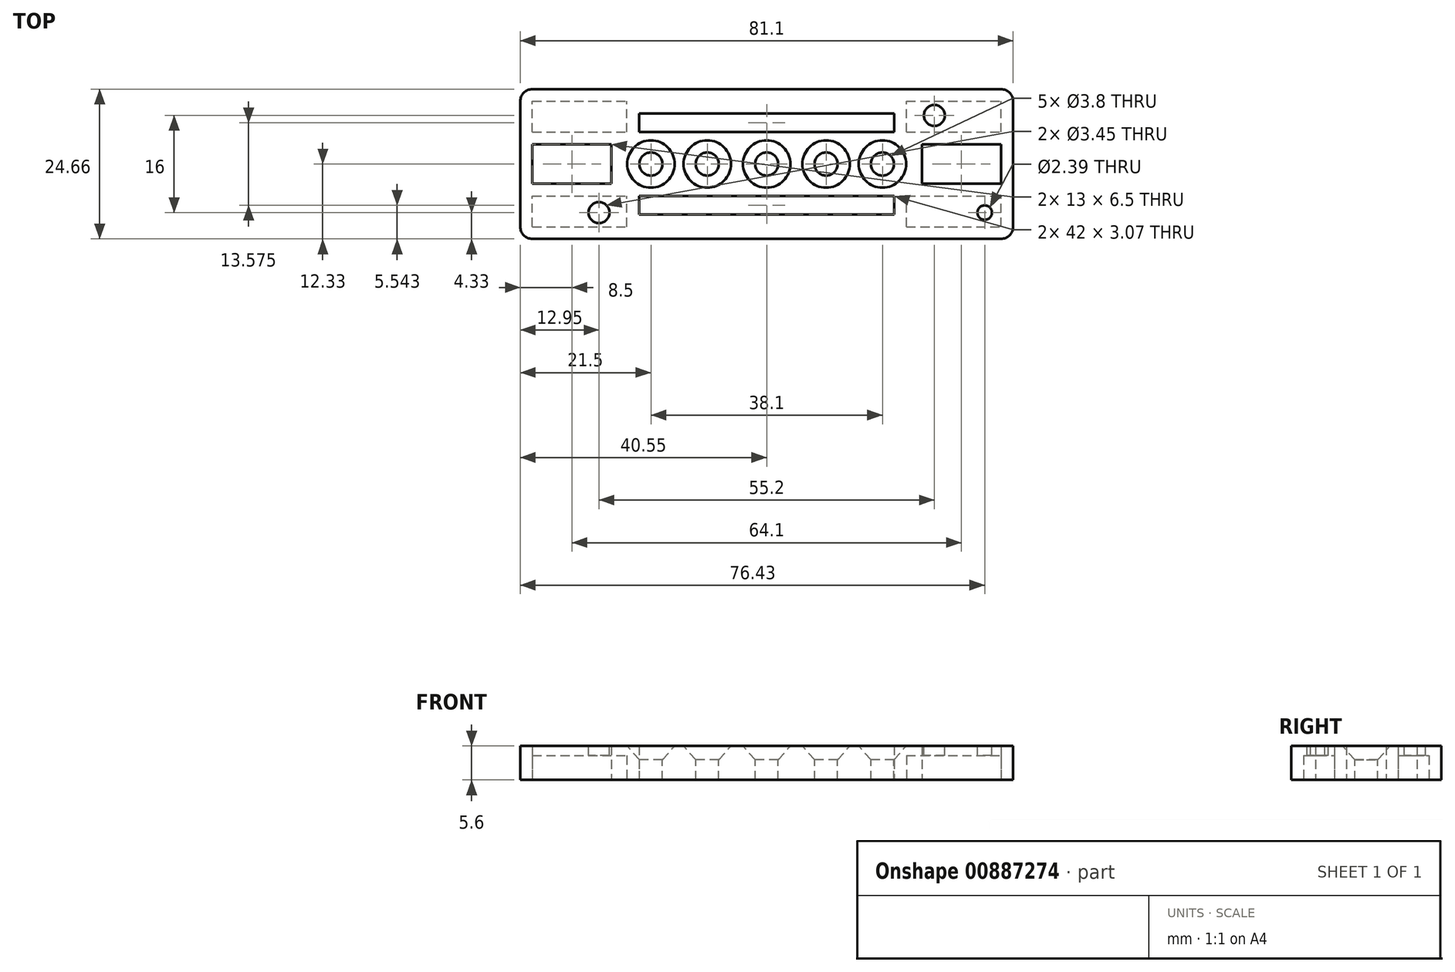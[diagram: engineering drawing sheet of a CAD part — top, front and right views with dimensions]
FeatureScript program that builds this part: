
annotation { "Feature Type Name" : "Feature", "Feature Type Description" : "" }
export const myFeature = defineFeature(function(context is Context, id is Id, definition is map)
    precondition{}
    {
        {
            var Q0;
            Q0=qCreatedBy(makeId("Top.planeOp"),FACE);
            var sketch = newSketch(context, id + "F0", { "sketchPlane" : qUnion([Q0])});
            skLineSegment(sketch, "E0.left", {"start": v(40.55, -12.33) * mm, "end": v(40.55, 12.32) * mm});
            skPoint(sketch, "E0.middle", {"position": v(0, 0) * mm});
            skLineSegment(sketch, "E1.bottom", {"start": v(-40.55, 12.33) * mm, "end": v(40.55, 12.32) * mm});
            skLineSegment(sketch, "E1.top", {"start": v(-40.55, -12.32) * mm, "end": v(40.55, -12.32) * mm});
            skLineSegment(sketch, "E1.left", {"start": v(-40.55, 12.33) * mm, "end": v(-40.55, -12.32) * mm});
            skLineSegment(sketch, "E2.bottom", {"start": v(38.55, -10.33) * mm, "end": v(-38.55, -10.32) * mm, "construction": true});
            skLineSegment(sketch, "E2.top", {"start": v(38.55, 10.32) * mm, "end": v(-38.55, 10.33) * mm, "construction": true});
            skLineSegment(sketch, "E2.left", {"start": v(38.55, -10.33) * mm, "end": v(38.55, 10.32) * mm, "construction": true});
            skLineSegment(sketch, "E2.right", {"start": v(-38.55, -10.32) * mm, "end": v(-38.55, 10.33) * mm, "construction": true});
            skSolve(sketch);
        }
        {
            var Q0;
            Q0=makeQuery(id+"F0.imprint","IMPRINT",FACE,{"disambiguationData":[TD([[makeQuery(id+"F0.imprint","IMPRINT",EDGE,{"derivedFrom":sQuery(id+"F0.wireOp",EDGE,"0eb0cbb2-3808-4bd1-ae6b-da4b1fe55920")}),-1.0]])]});
            var Q1;
            Q1=makeQuery(id+"F0.imprint","IMPRINT",FACE,{"disambiguationData":[TD([[makeQuery(id+"F0.imprint","IMPRINT",EDGE,{"derivedFrom":sQuery(id+"F0.wireOp",EDGE,"E0.left")}),1.0]])]});
            extrude(context, id + "F1", {"entities" : qUnion([Q0, Q1]), "depth" : 5.6 * mm, "offsetDistance" : 25 * mm});
        }
        {
            var Q0;
            Q0=makeQuery(id+"F1.opExtrude","CAP_FACE",FACE,{"disambiguationData":[OSD([sQuery(id+"F0.wireOp",EDGE,"E0.left"),sQuery(id+"F0.wireOp",EDGE,"E1.bottom"),sQuery(id+"F0.wireOp",EDGE,"E1.top"),sQuery(id+"F0.wireOp",EDGE,"E1.left")])],"isStart":false});
            var sketch = newSketch(context, id + "F2", { "sketchPlane" : qUnion([Q0])});
            skLineSegment(sketch, "E3.0.0", {"start": v(40.55, 12.32) * mm, "end": v(-40.55, 12.33) * mm});
            skLineSegment(sketch, "E3.0.1", {"start": v(-40.55, 12.33) * mm, "end": v(-40.55, -12.32) * mm});
            skLineSegment(sketch, "E3.0.2", {"start": v(-40.55, -12.32) * mm, "end": v(40.55, -12.32) * mm});
            skLineSegment(sketch, "E3.0.3", {"start": v(40.55, -12.32) * mm, "end": v(40.55, 12.32) * mm});
            skLineSegment(sketch, "E4.bottom", {"start": v(35.88, -8) * mm, "end": v(-27.6, -8) * mm, "construction": true});
            skLineSegment(sketch, "E4.top", {"start": v(27.6, 8) * mm, "end": v(-27.6, 8) * mm, "construction": true});
            skLineSegment(sketch, "E4.right", {"start": v(-27.6, -8) * mm, "end": v(-27.6, 8) * mm, "construction": true});
            skLineSegment(sketch, "E5", {"start": v(-27.6, 8) * mm, "end": v(-27.6, 12.33) * mm, "construction": true});
            skLineSegment(sketch, "E6", {"start": v(-27.6, -8) * mm, "end": v(-27.6, -12.32) * mm, "construction": true});
            skLineSegment(sketch, "E7", {"start": v(-27.6, 8) * mm, "end": v(-40.55, 8) * mm, "construction": true});
            skLineSegment(sketch, "E8", {"start": v(27.6, 8) * mm, "end": v(40.55, 8) * mm, "construction": true});
            skSolve(sketch);
        }
        {
            var Q0;
            Q0=sQuery(id+"F2.wireOp",VERTEX,"E4.bottom.end");
            var Q1;
            Q1=sQuery(id+"F2.wireOp",VERTEX,"E4.top.start");
            var Q2;
            Q2=makeQuery(id+"F1.opExtrude","SWEPT_BODY",BODY,{"disambiguationData":[OSD([sQuery(id+"F0.wireOp",EDGE,"E0.left"),sQuery(id+"F0.wireOp",EDGE,"E1.bottom"),sQuery(id+"F0.wireOp",EDGE,"E1.top"),sQuery(id+"F0.wireOp",EDGE,"E1.left")])]});
            hole(context, id + "F3", {"style" : HoleStyle.SIMPLE, "endStyle" : HoleEndStyle.THROUGH, "holeDiameter" : 3.45 * mm, "majorDiameter" : 5 * mm, "isTappedThrough" : true, "tappedDepth" : 12 * mm, "tapClearance" : 3, "locations" : qUnion([Q0, Q1]), "scope" : qUnion([Q2])});
        }
        {
            var Q0;
            Q0=sQuery(id+"F2.wireOp",VERTEX,"E4.bottom.start");
            var Q1;
            Q1=makeQuery(id+"F1.opExtrude","SWEPT_BODY",BODY,{"disambiguationData":[OSD([sQuery(id+"F0.wireOp",EDGE,"E0.left"),sQuery(id+"F0.wireOp",EDGE,"E1.bottom"),sQuery(id+"F0.wireOp",EDGE,"E1.top"),sQuery(id+"F0.wireOp",EDGE,"E1.left")])]});
            hole(context, id + "F4", {"style" : HoleStyle.SIMPLE, "endStyle" : HoleEndStyle.THROUGH, "holeDiameter" : 2.4 * mm, "majorDiameter" : 5 * mm, "isTappedThrough" : true, "tappedDepth" : 12 * mm, "tapClearance" : 3, "locations" : qUnion([Q0]), "scope" : qUnion([Q1])});
        }
        {
            var Q0;
            Q0=makeQuery(id+"F2.imprint","IMPRINT",FACE,{"disambiguationData":[TD([[makeQuery(id+"F2.imprint","IMPRINT",EDGE,{"derivedFrom":sQuery(id+"F2.wireOp",EDGE,"E3.0.0")}),-1.0]])]});
            var sketch = newSketch(context, id + "F5", { "sketchPlane" : qUnion([Q0])});
            skLineSegment(sketch, "E9", {"start": v(0, 0) * mm, "end": v(-9.78, 0) * mm, "construction": true});
            skLineSegment(sketch, "E10", {"start": v(-9.78, 0) * mm, "end": v(-19.05, 0) * mm, "construction": true});
            skLineSegment(sketch, "E11", {"start": v(0, 0) * mm, "end": v(9.78, 0) * mm, "construction": true});
            skLineSegment(sketch, "E12", {"start": v(9.78, 0) * mm, "end": v(19.05, 0) * mm, "construction": true});
            skSolve(sketch);
        }
        {
            var Q0;
            Q0=sQuery(id+"F5.wireOp",VERTEX,"E10.end");
            var Q1;
            Q1=sQuery(id+"F5.wireOp",VERTEX,"E9.end");
            var Q2;
            Q2=sQuery(id+"F5.wireOp",VERTEX,"E9.start");
            var Q3;
            Q3=sQuery(id+"F5.wireOp",VERTEX,"E11.end");
            var Q4;
            Q4=sQuery(id+"F5.wireOp",VERTEX,"E12.end");
            var Q5;
            Q5=makeQuery(id+"F1.opExtrude","SWEPT_BODY",BODY,{"disambiguationData":[OSD([sQuery(id+"F0.wireOp",EDGE,"E0.left"),sQuery(id+"F0.wireOp",EDGE,"E1.bottom"),sQuery(id+"F0.wireOp",EDGE,"E1.top"),sQuery(id+"F0.wireOp",EDGE,"E1.left")])]});
            hole(context, id + "F6", {"style" : HoleStyle.C_SINK, "endStyle" : HoleEndStyle.THROUGH, "holeDiameter" : 3.8 * mm, "cSinkDiameter" : 7.8 * mm, "cSinkAngle" : 82 * degree, "majorDiameter" : 5 * mm, "isTappedThrough" : true, "tappedDepth" : 12 * mm, "tapClearance" : 3, "locations" : qUnion([Q0, Q1, Q2, Q3, Q4]), "scope" : qUnion([Q5])});
        }
        {
            var Q0;
            Q0=makeQuery(id+"F1.opExtrude","CAP_FACE",FACE,{"disambiguationData":[OSD([sQuery(id+"F0.wireOp",EDGE,"E0.left"),sQuery(id+"F0.wireOp",EDGE,"E1.bottom"),sQuery(id+"F0.wireOp",EDGE,"E1.top"),sQuery(id+"F0.wireOp",EDGE,"E1.left")])],"isStart":true});
            var sketch = newSketch(context, id + "F7", { "sketchPlane" : qUnion([Q0])});
            skLineSegment(sketch, "E13.0.0", {"start": v(-40.55, -12.33) * mm, "end": v(40.55, -12.32) * mm});
            skLineSegment(sketch, "E13.0.1", {"start": v(40.55, -12.32) * mm, "end": v(40.55, 12.33) * mm});
            skLineSegment(sketch, "E13.0.2", {"start": v(40.55, 12.32) * mm, "end": v(-40.55, 12.32) * mm});
            skLineSegment(sketch, "E13.0.3", {"start": v(-40.55, 12.32) * mm, "end": v(-40.55, -12.33) * mm});
            skLineSegment(sketch, "E14", {"start": v(-40.55, 5.25) * mm, "end": v(40.55, 5.25) * mm});
            skLineSegment(sketch, "E15", {"start": v(-40.55, -5.25) * mm, "end": v(40.55, -5.25) * mm});
            skLineSegment(sketch, "E16.bottom", {"start": v(-38.55, 10.32) * mm, "end": v(38.55, 10.32) * mm});
            skLineSegment(sketch, "E16.top", {"start": v(-38.55, -10.33) * mm, "end": v(38.55, -10.32) * mm});
            skLineSegment(sketch, "E16.left", {"start": v(-38.55, 10.32) * mm, "end": v(-38.55, -10.33) * mm});
            skLineSegment(sketch, "E16.right", {"start": v(38.55, 10.33) * mm, "end": v(38.55, -10.32) * mm});
            skLineSegment(sketch, "E17", {"start": v(-23, 10.32) * mm, "end": v(-23, 5.25) * mm});
            skLineSegment(sketch, "E18", {"start": v(-21, 10.32) * mm, "end": v(-21, 5.25) * mm});
            skLineSegment(sketch, "E19", {"start": v(21, 10.33) * mm, "end": v(21, 5.25) * mm});
            skLineSegment(sketch, "E20", {"start": v(23, 10.33) * mm, "end": v(23, 5.25) * mm});
            skLineSegment(sketch, "E21", {"start": v(21, -5.25) * mm, "end": v(21, -10.32) * mm});
            skLineSegment(sketch, "E22", {"start": v(23, -5.25) * mm, "end": v(23, -10.32) * mm});
            skLineSegment(sketch, "E23", {"start": v(23.55, 5.25) * mm, "end": v(23.55, -5.25) * mm});
            skLineSegment(sketch, "E24", {"start": v(-23.55, 5.25) * mm, "end": v(-23.55, -5.25) * mm});
            skLineSegment(sketch, "E25.bottom", {"start": v(-38.55, 3.25) * mm, "end": v(-25.55, 3.25) * mm});
            skLineSegment(sketch, "E25.top", {"start": v(-38.55, -3.25) * mm, "end": v(-25.55, -3.25) * mm});
            skLineSegment(sketch, "E25.right", {"start": v(-25.55, 3.25) * mm, "end": v(-25.55, -3.25) * mm});
            skLineSegment(sketch, "E26.bottom", {"start": v(25.55, 3.25) * mm, "end": v(38.55, 3.25) * mm});
            skLineSegment(sketch, "E26.top", {"start": v(25.55, -3.25) * mm, "end": v(38.55, -3.25) * mm});
            skLineSegment(sketch, "E26.left", {"start": v(25.55, 3.25) * mm, "end": v(25.55, -3.25) * mm});
            skLineSegment(sketch, "E27", {"start": v(-23, -5.25) * mm, "end": v(-23, -10.33) * mm});
            skLineSegment(sketch, "E28", {"start": v(-21, -5.25) * mm, "end": v(-21, -10.33) * mm});
            skLineSegment(sketch, "E29", {"start": v(-40.55, 0) * mm, "end": v(40.55, 0) * mm, "construction": true});
            skLineSegment(sketch, "E30", {"start": v(-23.44, 5.25) * mm, "end": v(-23.44, 0) * mm, "construction": true});
            skLineSegment(sketch, "E31", {"start": v(-23.44, 0) * mm, "end": v(-23.44, -5.25) * mm, "construction": true});
            skLineSegment(sketch, "E32", {"start": v(0, 12.32) * mm, "end": v(0, -12.32) * mm, "construction": true});
            skLineSegment(sketch, "E33", {"start": v(-21, 7.79) * mm, "end": v(0, 7.79) * mm, "construction": true});
            skLineSegment(sketch, "E34", {"start": v(0, 7.79) * mm, "end": v(21, 7.79) * mm, "construction": true});
            skLineSegment(sketch, "E35", {"start": v(-21, 8.32) * mm, "end": v(21, 8.33) * mm});
            skLineSegment(sketch, "E36", {"start": v(-21, -8.33) * mm, "end": v(21, -8.32) * mm});
            skSolve(sketch);
        }
        {
            var Q0;
            {var subQ5=sQuery(id+"F7.wireOp",EDGE,"E17");Q0=makeQuery(id+"F7.imprint","IMPRINT",FACE,{"disambiguationData":[TD([[makeQuery(id+"F7.imprint","IMPRINT",EDGE,{"derivedFrom":subQ5}),-1.0]])]});}
            var Q1;
            {var subQ6=sQuery(id+"F7.wireOp",EDGE,"E27");Q1=makeQuery(id+"F7.imprint","IMPRINT",FACE,{"disambiguationData":[TD([[makeQuery(id+"F7.imprint","IMPRINT",EDGE,{"derivedFrom":subQ6}),-1.0]])]});}
            var Q2;
            {var subQ5=sQuery(id+"F7.wireOp",EDGE,"E22");Q2=makeQuery(id+"F7.imprint","IMPRINT",FACE,{"disambiguationData":[TD([[makeQuery(id+"F7.imprint","IMPRINT",EDGE,{"derivedFrom":subQ5}),1.0]])]});}
            var Q3;
            {var subQ5=sQuery(id+"F7.wireOp",EDGE,"E20");Q3=makeQuery(id+"F7.imprint","IMPRINT",FACE,{"disambiguationData":[TD([[makeQuery(id+"F7.imprint","IMPRINT",EDGE,{"derivedFrom":subQ5}),1.0]])]});}
            var Q4;
            Q4=makeQuery(id+"F1.opExtrude","CAP_FACE",FACE,{"disambiguationData":[OSD([sQuery(id+"F0.wireOp",EDGE,"E0.left"),sQuery(id+"F0.wireOp",EDGE,"E1.bottom"),sQuery(id+"F0.wireOp",EDGE,"E1.top"),sQuery(id+"F0.wireOp",EDGE,"E1.left")])],"isStart":false});
            extrude(context, id + "F8", {"entities" : qUnion([Q0, Q1, Q2, Q3]), "operationType" : NewBodyOperationType.REMOVE, "endBound" : BoundingType.UP_TO_SURFACE, "oppositeDirection" : true, "depth" : 25 * mm, "endBoundEntityFace" : qUnion([Q4]), "hasOffset" : true, "offsetDistance" : 1.6 * mm});
        }
        {
            var Q0;
            {var subQ5=sQuery(id+"F7.wireOp",EDGE,"E36");Q0=makeQuery(id+"F7.imprint","IMPRINT",FACE,{"disambiguationData":[TD([[makeQuery(id+"F7.imprint","IMPRINT",EDGE,{"derivedFrom":subQ5}),1.0]])]});}
            var Q1;
            {var subQ0=sQuery(id+"F7.wireOp",EDGE,"E25.bottom");Q1=makeQuery(id+"F7.imprint","IMPRINT",FACE,{"disambiguationData":[TD([[makeQuery(id+"F7.imprint","IMPRINT",EDGE,{"derivedFrom":subQ0}),-1.0]])]});}
            var Q2;
            {var subQ0=sQuery(id+"F7.wireOp",EDGE,"E26.bottom");Q2=makeQuery(id+"F7.imprint","IMPRINT",FACE,{"disambiguationData":[TD([[makeQuery(id+"F7.imprint","IMPRINT",EDGE,{"derivedFrom":subQ0}),-1.0]])]});}
            var Q3;
            {var subQ5=sQuery(id+"F7.wireOp",EDGE,"E35");Q3=makeQuery(id+"F7.imprint","IMPRINT",FACE,{"disambiguationData":[TD([[makeQuery(id+"F7.imprint","IMPRINT",EDGE,{"derivedFrom":subQ5}),-1.0]])]});}
            var Q4;
            Q4=makeQuery(id+"F1.opExtrude","CAP_FACE",FACE,{"disambiguationData":[OSD([sQuery(id+"F0.wireOp",EDGE,"E0.left"),sQuery(id+"F0.wireOp",EDGE,"E1.bottom"),sQuery(id+"F0.wireOp",EDGE,"E1.top"),sQuery(id+"F0.wireOp",EDGE,"E1.left")])],"isStart":false});
            extrude(context, id + "F9", {"entities" : qUnion([Q0, Q1, Q2, Q3]), "operationType" : NewBodyOperationType.REMOVE, "endBound" : BoundingType.UP_TO_SURFACE, "oppositeDirection" : true, "depth" : 25 * mm, "endBoundEntityFace" : qUnion([Q4]), "offsetDistance" : 25 * mm});
        }
        {
            var Q0;
            Q0=makeQuery(id+"F1.opExtrude","SWEPT_EDGE",EDGE,{"disambiguationData":[OSD([sQuery(id+"F0.wireOp",EDGE,"E0.left"),sQuery(id+"F0.wireOp",EDGE,"E1.bottom")])]});
            var Q1;
            Q1=makeQuery(id+"F1.opExtrude","SWEPT_EDGE",EDGE,{"disambiguationData":[OSD([sQuery(id+"F0.wireOp",EDGE,"E1.bottom"),sQuery(id+"F0.wireOp",EDGE,"E1.left")])]});
            var Q2;
            Q2=makeQuery(id+"F1.opExtrude","SWEPT_EDGE",EDGE,{"disambiguationData":[OSD([sQuery(id+"F0.wireOp",EDGE,"E1.top"),sQuery(id+"F0.wireOp",EDGE,"E1.left")])]});
            var Q3;
            Q3=makeQuery(id+"F1.opExtrude","SWEPT_EDGE",EDGE,{"disambiguationData":[OSD([sQuery(id+"F0.wireOp",EDGE,"E0.left"),sQuery(id+"F0.wireOp",EDGE,"E1.top")])]});
            fillet(context, id + "F10", {"entities" : qUnion([Q0, Q1, Q2, Q3]), "radius" : 2 * mm, "tangentPropagation" : true, "allowEdgeOverflow" : false});
        }
    });
